# Revit family: Difusores abiertos para falsos suelos y falsos techos
name_source: partatom
category: Rociadores
revit_build: Autodesk Revit 2017 (Build: 20160225_1515(x64)
units: mm (PartAtom-declared; Revit-internal decimal feet)

## family parameters
Compartido = No
Corte con vacíos al cargar = No
Cota de conector redondo = Radio de uso
Mantener orientación de anotación = No
Número OmniClass = 23.65.70.17.11.24
Punto de cálculo de habitación = No
Se basa en plano de trabajo = Sí
Siempre vertical = Sí
Tipo de pieza = Normal
Título OmniClass = Fire Fighting Sprinkler Heads

## types (1)
- Difusor abierto 6 toberas - 2,4 a 30,6 l/min
    Clase de presión = Norma
    Cobertura = Norma
    Descripción = Cabeza nebulizadora abierta para instalación en tubería seca, fabricada en acero inoxidable AISI 304 para alta presión.
Equipada con 4 o 6  toberas en horizontal en un ángulo de apertura de 360º.
    Elevación por defecto = 1219 mm
    Fabricante = Aguilera Electrónica
    Flujo = 2.4 L/min
    Flujo máximo = 30.6 L/min
    Flujo mínimo = 2.4 L/min
    Modelo = AN/CA360T6
    Orificio = Norma
    Respuesta = Norma
    Símbolo = Sí
    Símbolo texto modelo = Sí
    URL = http://aguilera.es
    Zona de acción = Sí
